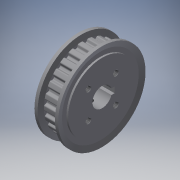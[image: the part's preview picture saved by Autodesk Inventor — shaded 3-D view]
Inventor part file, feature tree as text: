
AUTODESK INVENTOR PART (.ipt)
format: ipt  version: 2017 (Build 210142000, 142)  size: 589,824 bytes
history: native  units: mm
features: other x14, revolve x4, hole x2, extrude x2, thread x2, sketch x2, pattern_linear x1
ambient origin geometry x8: Origin, YZ Plane, XZ Plane, XY Plane, X Axis, Y Axis, Z Axis, Center Point
bodies: Solid1 (feature_tree)
feature tree (27):
  revolve  "Revolution1"  [1 undecoded]
  hole  "Hole1"  [1 undecoded]
  extrude  "Extrusion1"  TaperAngle=360.0deg  [1 undecoded]
  extrude  "Extrusion2"  TaperAngle=360.0deg  [1 undecoded]
  revolve  "Revolution2"  [1 undecoded]
  revolve  "Revolution3"  Angle=360.0deg
  thread  "Thread1"  [1 undecoded]
  revolve  "Revolution4"  [1 undecoded]
  thread  "Thread2"  [1 undecoded]
  hole  "Hole2"  [1 undecoded]
  pattern_linear  "Rectangular Pattern1"  [2 undecoded]
  other  "to_screw1_XY"
  other  "to_screw1_YZ"
  other  "to_screw1_ZX"
  other  "to_screw1_X"
  other  "to_screw1_Y"
  other  "to_screw1_Z"
  other  "to_screw1_Center"
  other  "to_screw2_XY"
  other  "to_screw2_YZ"
  other  "to_screw2_ZX"
  other  "to_screw2_X"
  other  "to_screw2_Y"
  other  "to_screw2_Z"
  other  "to_screw2_Center"
  sketch  "Sketch2"  dims[d0=360.0deg]
  sketch  "Sketch8"  dims[d1=10.0mm d2=6.0mm d3=4.0mm d4=2.0mm d5=90.0deg d6=12.5mm d7=0.0mm d8=7.5mm d9=0.0mm d10=12.5mm d11=0.0mm d12=360.0deg d13=360.0deg d14=13.56mm d15=0.0mm d16=360.0deg d17=14.96mm d18=0.0mm d19=2.459mm d20=6.2705mm d21=3.0mm d22=2.0mm d23=90.0deg d24=8.790148mm d25=120.0deg d26=20.0mm d28=14.142136mm d29=20.0mm d31=14.142136mm d32=0.0mm]
note: 11 required parameter values undecoded (feature->parameter linkage not recoverable at this tier; creation-order binding heuristic only, values carry confidence <= 0.55)